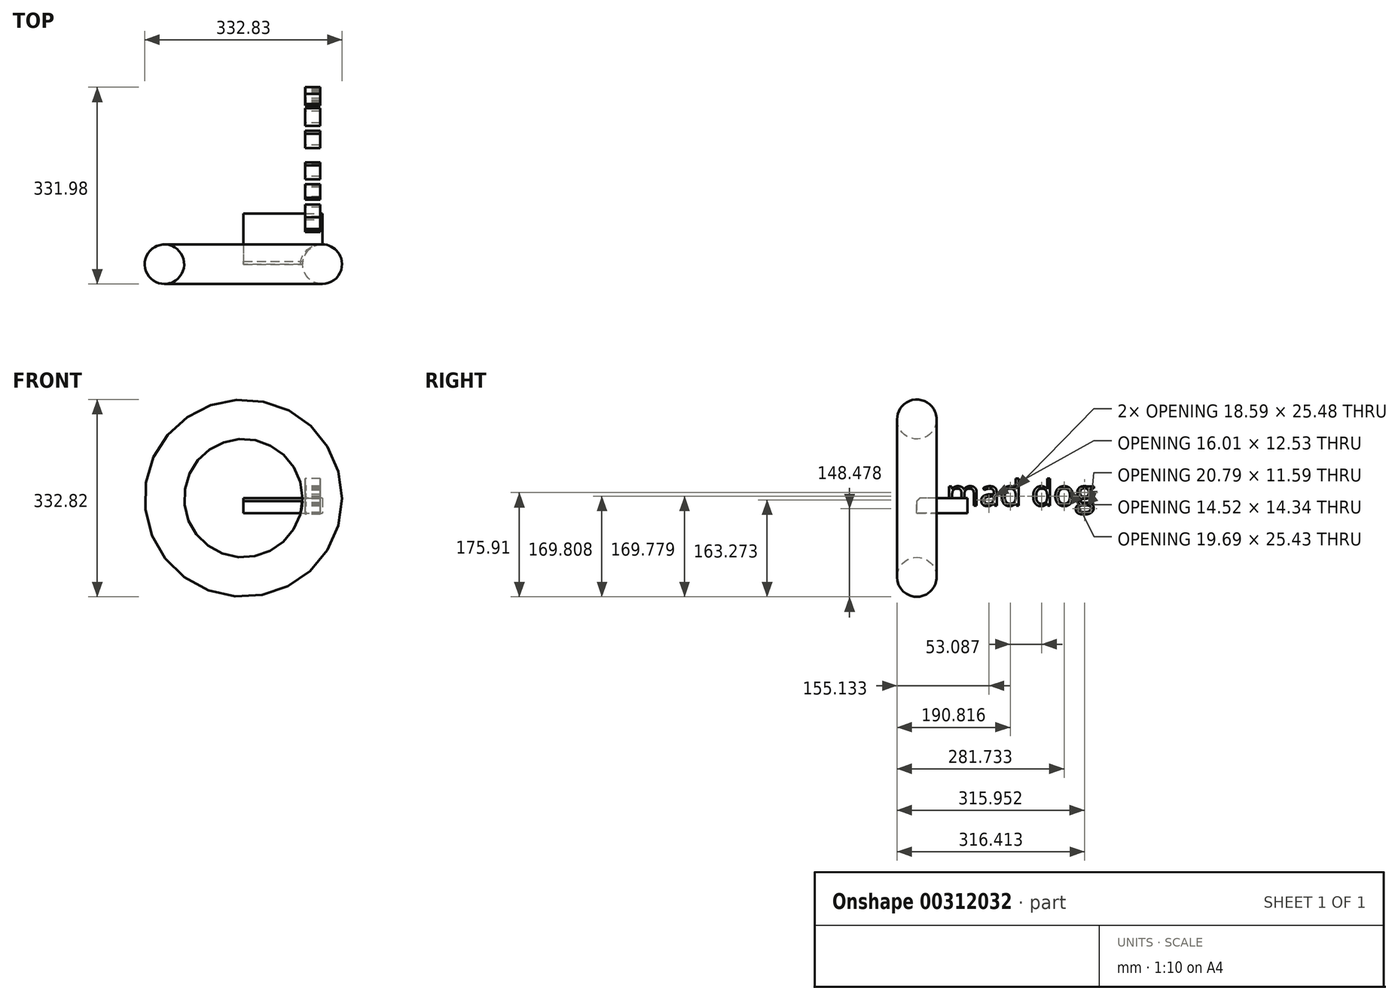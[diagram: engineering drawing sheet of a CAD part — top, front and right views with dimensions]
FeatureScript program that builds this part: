
annotation { "Feature Type Name" : "Feature", "Feature Type Description" : "" }
export const myFeature = defineFeature(function(context is Context, id is Id, definition is map)
    precondition{}
    {
        {
            var Q0;
            Q0=qCreatedBy(makeId("Top.planeOp"),FACE);
            var sketch = newSketch(context, id + "F0", { "sketchPlane" : qUnion([Q0])});
            skLineSegment(sketch, "E0.bottom", {"start": v(-104.47, 40.25) * mm, "end": v(28.64, 40.25) * mm});
            skLineSegment(sketch, "E0.top", {"start": v(-104.47, -45.35) * mm, "end": v(28.64, -45.35) * mm});
            skLineSegment(sketch, "E0.left", {"start": v(-104.47, 40.25) * mm, "end": v(-104.47, -45.35) * mm});
            skLineSegment(sketch, "E0.right", {"start": v(28.64, 40.25) * mm, "end": v(28.64, -45.35) * mm});
            skSolve(sketch);
        }
        {
            var Q0;
            Q0=makeQuery(id+"F0.imprint","IMPRINT",FACE,{"disambiguationData":[TD([[makeQuery(id+"F0.imprint","IMPRINT",EDGE,{"derivedFrom":sQuery(id+"F0.wireOp",EDGE,"E0.bottom")}),-1.0]])]});
            extrude(context, id + "F1", {"entities" : qUnion([Q0]), "depth" : 25.4 * mm});
        }
        {
            var Q0;
            Q0=makeQuery(id+"F1.opExtrude","CAP_FACE",FACE,{"disambiguationData":[OSD([sQuery(id+"F0.wireOp",EDGE,"E0.bottom"),sQuery(id+"F0.wireOp",EDGE,"E0.top"),sQuery(id+"F0.wireOp",EDGE,"E0.left"),sQuery(id+"F0.wireOp",EDGE,"E0.right")])],"isStart":false});
            var sketch = newSketch(context, id + "F2", { "sketchPlane" : qUnion([Q0])});
            skCircle(sketch, "E1", {"center": v(28.64, -45.35) * mm, "radius": 33.3 * mm});
            skSolve(sketch);
        }
        {
            var Q0;
            Q0 = qSketchRegion(id + "F2", true);
            var Q1;
            Q1=makeQuery(id+"F1.opExtrude","CAP_EDGE",EDGE,{"disambiguationData":[OSD([sQuery(id+"F0.wireOp",EDGE,"E0.left")])],"isStart":false});
            revolve(context, id + "F3", {"operationType" : NewBodyOperationType.ADD, "entities" : qUnion([Q0]), "axis" : qUnion([Q1]), "revolveType" : RevolveType.FULL});
        }
        {
            var Q0;
            Q0=makeQuery(id+"F1.opExtrude","CAP_EDGE",EDGE,{"disambiguationData":[OSD([sQuery(id+"F0.wireOp",EDGE,"E0.top")])],"isStart":false});
            chamfer(context, id + "F4", {"entities" : qUnion([Q0]), "width" : 5.08 * mm, "tangentPropagation" : true});
        }
        {
            var Q0;
            Q0=qCreatedBy(makeId("Right.planeOp"),FACE);
            var sketch = newSketch(context, id + "F5", { "sketchPlane" : qUnion([Q0])});
            skText(sketch, "E2", { "text": "mad dog", "fontName": "OpenSans-Regular.ttf"});
            const initialGuessF5  = {"E2": [0.00393, 0.01252, 1, 0, 0.0438]};
            skSetInitialGuess(sketch, initialGuessF5);
            skSolve(sketch);
        }
        {
            var Q0;
            Q0 = qSketchRegion(id + "F5", true);
            extrude(context, id + "F6", {"entities" : qUnion([Q0]), "operationType" : NewBodyOperationType.ADD, "depth" : 25.4 * mm});
        }
    });
